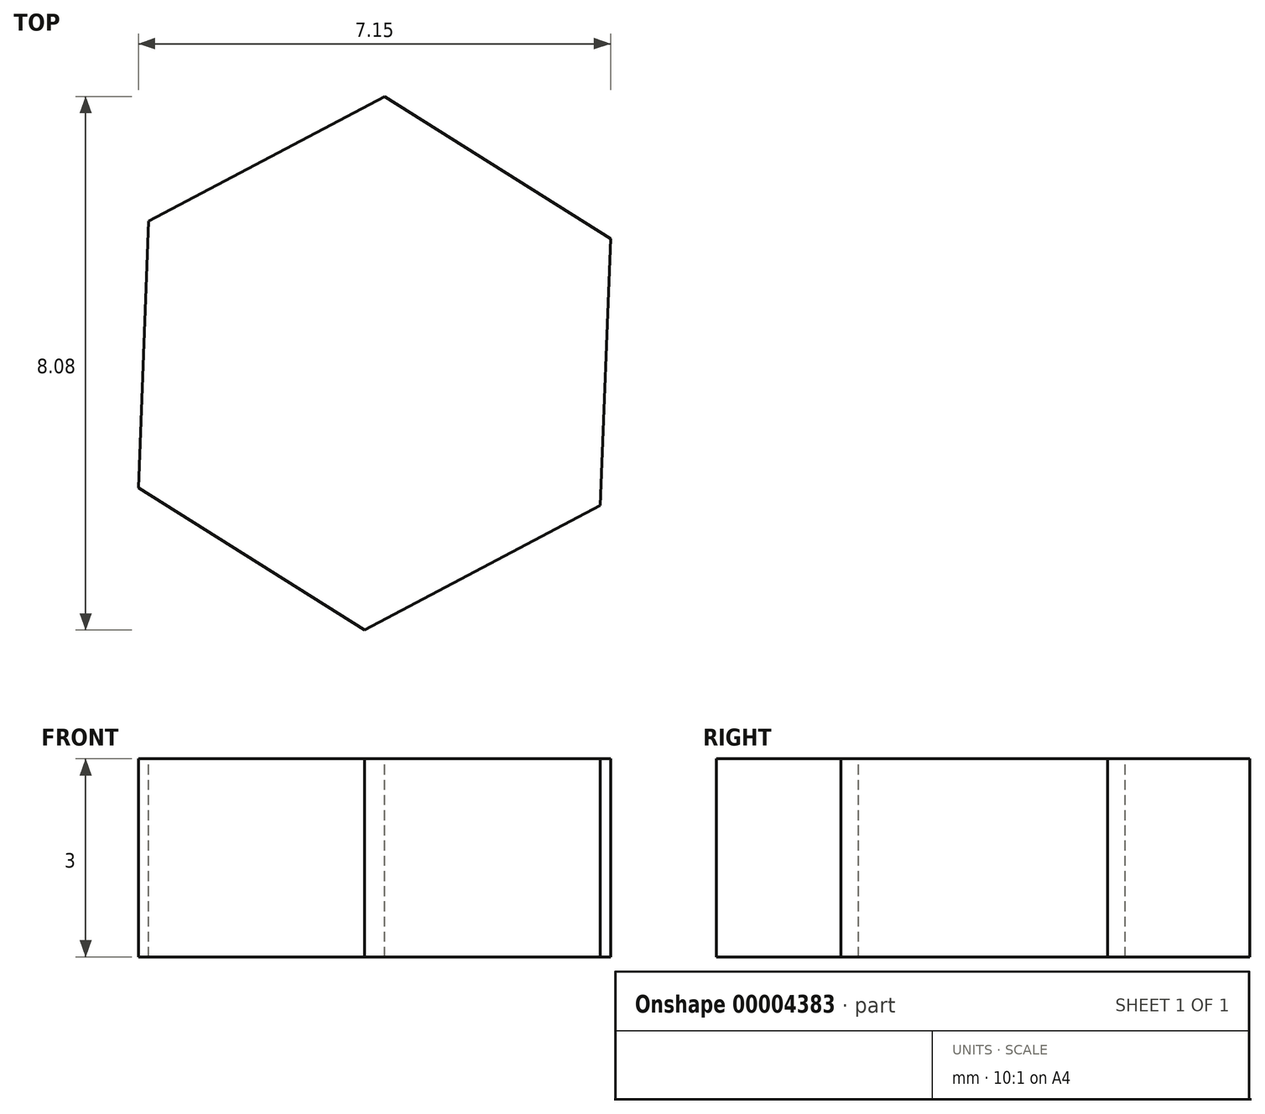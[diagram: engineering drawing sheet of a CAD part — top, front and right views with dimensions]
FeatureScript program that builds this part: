
annotation { "Feature Type Name" : "Feature", "Feature Type Description" : "" }
export const myFeature = defineFeature(function(context is Context, id is Id, definition is map)
    precondition{}
    {
        {
            var Q0;
            Q0=qCreatedBy(makeId("Top.planeOp"),FACE);
            var sketch = newSketch(context, id + "F0", { "sketchPlane" : qUnion([Q0])});
            skCircle(sketch, "E0.cCircle", {"center": v(-3.57, 0) * mm, "radius": 4.04 * mm, "construction": true});
            skLineSegment(sketch, "E0.0", {"start": v(0, 1.89) * mm, "end": v(-0.15, -2.15) * mm});
            skLineSegment(sketch, "E0.1", {"start": v(-0.15, -2.15) * mm, "end": v(-3.73, -4.04) * mm});
            skLineSegment(sketch, "E0.2", {"start": v(-3.73, -4.04) * mm, "end": v(-7.15, -1.89) * mm});
            skLineSegment(sketch, "E0.3", {"start": v(-7.15, -1.89) * mm, "end": v(-7, 2.15) * mm});
            skLineSegment(sketch, "E0.4", {"start": v(-7, 2.15) * mm, "end": v(-3.42, 4.04) * mm});
            skLineSegment(sketch, "E0.5", {"start": v(-3.42, 4.04) * mm, "end": v(0, 1.89) * mm});
            skSolve(sketch);
        }
        {
            var Q0;
            Q0 = qSketchRegion(id + "F0", true);
            extrude(context, id + "F1", {"entities" : qUnion([Q0]), "oppositeDirection" : true, "depth" : 3 * mm});
        }
    });
